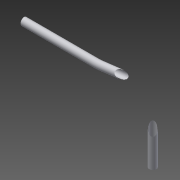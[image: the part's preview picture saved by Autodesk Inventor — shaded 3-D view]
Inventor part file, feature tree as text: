
AUTODESK INVENTOR PART (.ipt)
format: ipt  version: 2015 (Build 190159000, 159)  size: 192,000 bytes
history: native  units: mm
features: sketch x5, other x4, extrude x2, shell x1
ambient origin geometry x8: Origin, YZ Plane, XZ Plane, XY Plane, X Axis, Y Axis, Z Axis, Center Point
bodies: Body1 (feature_tree)
feature tree (12):
  other  "Bryła1"
  extrude  "Wyciągnięcie proste1"  Depth=32.0mm
  shell  "Skorupa1"  Thickness=815.0mm
  other  "Gięcie części1"
  sketch  "Szkic7"
  other  "Płaszczyzna konstrukcyjna4"
  other  "Gięcie części2"
  extrude  "Wyciągnięcie proste4"  Depth=2.0mm
  sketch  "Szkic1"
  sketch  "Szkic4"
  sketch  "Szkic8"
  sketch  "Szkic10"
